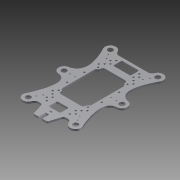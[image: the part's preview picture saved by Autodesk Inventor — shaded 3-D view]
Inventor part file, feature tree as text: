
AUTODESK INVENTOR PART (.ipt)
format: ipt  version: 2012 (Build 160160000, 160)  size: 548,352 bytes
history: native  units: mm
features: sketch x4, hole x3, extrude x2
ambient origin geometry x8: Origin, YZ Plane, XZ Plane, XY Plane, X Axis, Y Axis, Z Axis, Center Point
bodies: Solid1 (feature_tree)
feature tree (9):
  extrude  "Extrusion1"  Depth=3.0mm TaperAngle=0.0deg
  sketch  "Sketch2"  dims[d75=2.0mm d76=5.0mm d77=5.0mm d78=3.0mm d79=3.0mm d80=15.0mm d81=15.0mm d82=30.0mm d83=82.0mm d84=2.0mm d85=2.0mm d86=5.0mm d87=10.0mm d88=15.0mm d89=20.0mm d90=2.0mm d91=8.75mm d92=8.75mm d93=8.75mm d94=8.75mm d95=8.75mm d96=8.75mm d97=2.0mm d98=2.0mm d99=9.0mm d100=2.0mm d101=2.0mm d102=9.0mm d103=10.0mm d104=6.0mm d105=21.0mm d106=21.014083mm d107=21.014083mm d108=21.0mm d109=21.0mm d110=21.014083mm d111=21.0mm d112=21.014083mm d113=4.0mm d114=4.0mm d115=4.0mm d116=4.0mm d117=4.0mm d118=4.0mm d119=4.0mm d120=4.0mm d121=4.0mm d122=4.0mm d123=4.0mm d124=4.0mm d125=68.5mm d126=50.55mm d127=15.0mm d128=15.0mm d129=15.0mm d130=15.0mm d131=5.632993mm d132=10.75mm d133=10.0mm d134=10.0mm d135=4.7mm d136=5.0mm d137=5.0mm d138=5.0mm d139=10.8mm d140=10.0mm d141=4.7mm d142=5.0mm d143=5.0mm d144=10.0mm d145=5.0mm d146=5.0mm d147=5.682993mm d148=8.75mm d149=6.0mm d150=4.0mm d151=2.0mm d152=90.0deg d153=8.0mm d154=20.594885mm]
  hole  "Hole1"  [1 undecoded]
  hole  "Hole2"  [1 undecoded]
  hole  "Hole3"  [1 undecoded]
  extrude  "Extrusion2"  Depth=50.55mm
  sketch  "Sketch1"  dims[d0=2.0mm d1=5.0mm d2=5.0mm d5=15.0mm d6=15.0mm d7=30.0mm d8=82.0mm d9=2.0mm d10=2.0mm d12=10.0mm d13=15.0mm d14=20.0mm d15=2.0mm d29=6.0mm d38=4.0mm d39=4.0mm d40=4.0mm d42=4.0mm d44=4.0mm d45=4.0mm d46=4.0mm d47=4.0mm d48=4.0mm d49=4.0mm d73=3.0mm d74=0.0mm]
  sketch  "Sketch3"  dims[d155=2.0mm d156=5.0mm d157=5.0mm d158=3.0mm d159=3.0mm d160=15.0mm d161=15.0mm d162=30.0mm d163=82.0mm d164=2.0mm d165=2.0mm d166=5.0mm d167=10.0mm d168=15.0mm d169=20.0mm d170=2.0mm d171=8.75mm d172=8.75mm d173=8.75mm d174=8.75mm d175=8.75mm d176=8.75mm d177=2.0mm d178=2.0mm d179=9.0mm d180=2.0mm d181=2.0mm d182=9.0mm d183=10.0mm d184=6.0mm d185=21.0mm d186=21.014083mm d187=21.014083mm d188=21.0mm d189=21.0mm d190=21.014083mm d191=21.0mm d192=21.014083mm d193=4.0mm d194=4.0mm d195=4.0mm d196=4.0mm d197=4.0mm d198=4.0mm d199=4.0mm d200=4.0mm d201=4.0mm d202=4.0mm d203=4.0mm d204=4.0mm d205=68.5mm d206=50.55mm d207=15.0mm d208=15.0mm d209=15.0mm d210=15.0mm d211=5.632993mm d212=10.75mm d213=10.0mm d214=10.0mm d215=4.7mm d216=5.0mm d217=5.0mm d218=5.0mm d219=10.8mm d220=10.0mm d221=4.7mm d222=5.0mm d223=5.0mm d224=10.0mm d225=5.0mm d226=5.0mm d227=5.682993mm d228=3.0mm d229=6.0mm d230=4.0mm d231=2.0mm d232=90.0deg d233=8.0mm d234=20.594885mm]
  sketch  "Sketch4"  dims[d235=2.0mm d236=5.0mm d237=5.0mm d238=3.0mm d239=3.0mm d240=15.0mm d241=15.0mm d242=30.0mm d243=82.0mm d244=2.0mm d245=2.0mm d246=5.0mm d247=10.0mm d248=15.0mm d249=20.0mm d250=2.0mm d251=8.75mm d252=8.75mm d253=8.75mm d254=8.75mm d255=8.75mm d256=8.75mm d257=2.0mm d258=2.0mm d259=9.0mm d260=2.0mm d261=2.0mm d262=9.0mm d263=10.0mm d264=6.0mm d265=21.0mm d266=21.014083mm d267=21.014083mm d268=21.0mm d269=21.0mm d270=21.014083mm d271=21.0mm d272=21.014083mm d273=4.0mm d274=4.0mm d275=4.0mm d276=4.0mm d277=4.0mm d278=4.0mm d279=4.0mm d280=4.0mm d281=4.0mm d282=4.0mm d283=4.0mm d284=4.0mm d285=68.5mm d286=50.55mm d287=15.0mm d288=15.0mm d289=15.0mm d290=15.0mm d291=5.632993mm d292=10.75mm d293=10.0mm d294=10.0mm d295=4.7mm d296=5.0mm d297=5.0mm d298=5.0mm d299=10.8mm d300=10.0mm d301=4.7mm d302=5.0mm d303=5.0mm d304=10.0mm d305=5.0mm d306=5.0mm d307=5.682993mm d308=2.0mm d309=6.0mm d310=4.0mm d311=2.0mm d312=90.0deg d313=8.0mm d314=20.594885mm d324=3.0mm d325=0.0mm d326=50.55mm d327=68.5mm d328=50.55mm d329=68.5mm d330=50.55mm d331=68.5mm d332=3.0mm d333=5.0mm d334=5.0mm]
note: 3 required parameter values undecoded (feature->parameter linkage not recoverable at this tier; creation-order binding heuristic only, values carry confidence <= 0.55)
